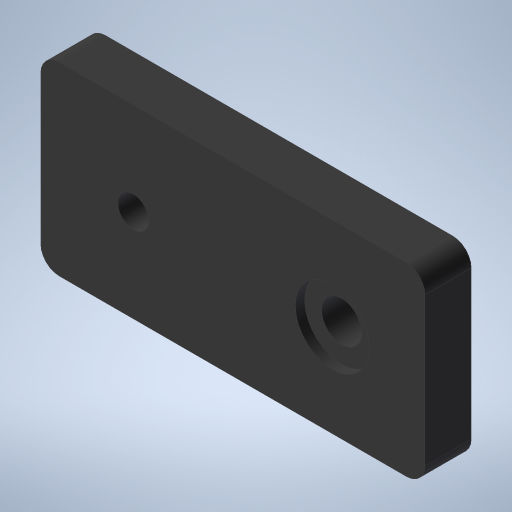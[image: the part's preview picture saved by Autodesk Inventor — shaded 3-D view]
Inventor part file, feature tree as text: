
AUTODESK INVENTOR PART (.ipt)
format: ipt  version: 2024.2 (Build 282272000, 272)  size: 212,992 bytes
history: native  units: in
note: dims shown in document units (in); Inventor stores cm internally (conversion verified against a paired STEP export)
features: extrude x2, sketch x2, fillet x1
ambient origin geometry x8: Origin, YZ Plane, XZ Plane, XY Plane, X Axis, Y Axis, Z Axis, Center Point
bodies: Solid1 (feature_tree)
feature tree (5):
  extrude  "Extrusion1"  Depth=1.6339in
  extrude  "Extrusion2"  Depth=0.7874in
  fillet  "Fillet1"  Radius=0.3937in
  sketch  "Sketch1"  dims[d0=1.6339in d1=0.1713in]
  sketch  "Sketch2"  dims[d2=0.1319in d3=0.7874in d4=0.3937in d5=0.3937in d6=0.4528in d7=0.1969in d8=0.0in d9=0.315in d10=0.0394in d11=0.0in d12=0.0787in]
